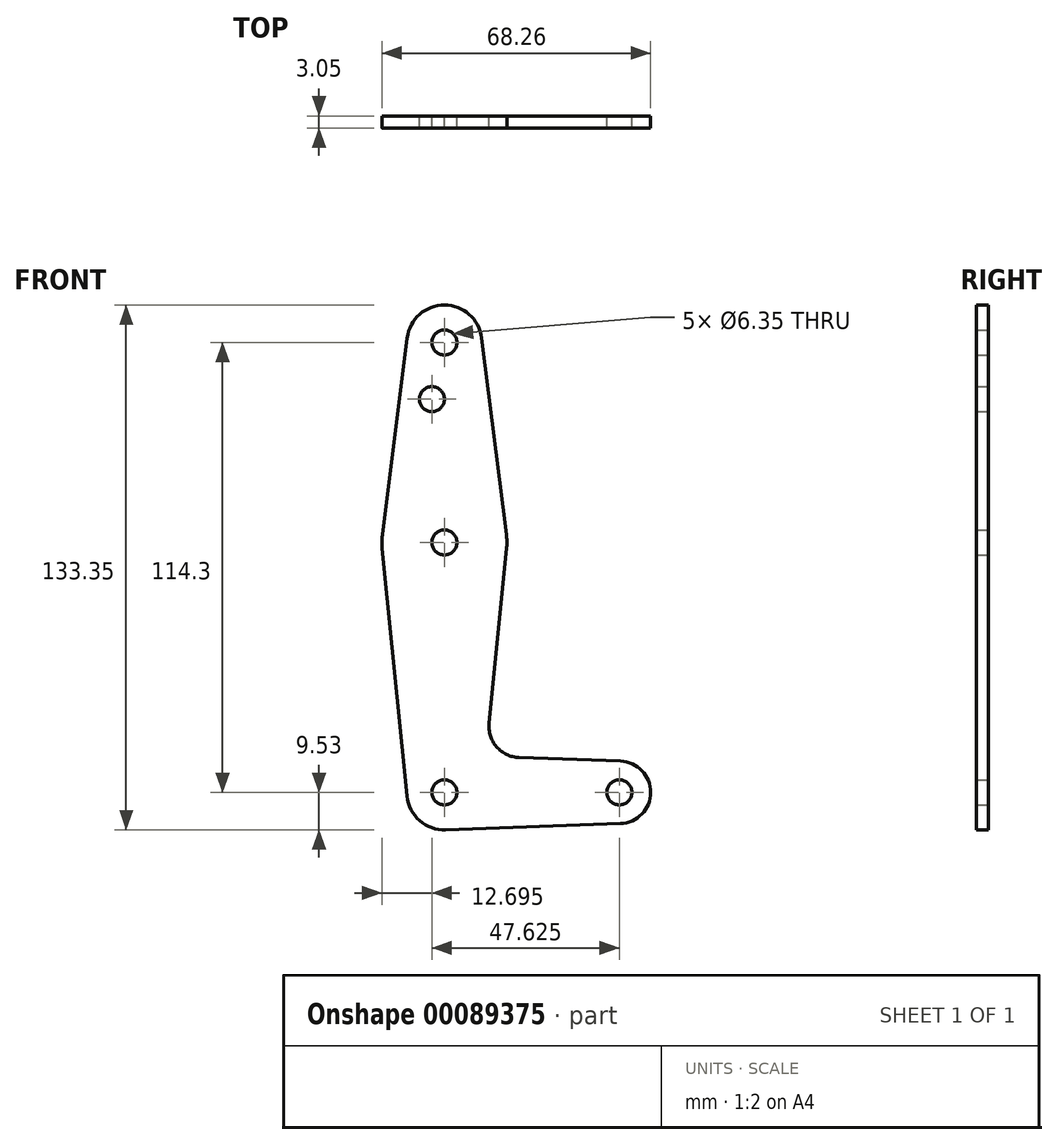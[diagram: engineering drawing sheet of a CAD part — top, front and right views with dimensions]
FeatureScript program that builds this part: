
annotation { "Feature Type Name" : "Feature", "Feature Type Description" : "" }
export const myFeature = defineFeature(function(context is Context, id is Id, definition is map)
    precondition{}
    {
        {
            var Q0;
            Q0=qCreatedBy(makeId("Front.planeOp"),FACE);
            var sketch = newSketch(context, id + "F0", { "sketchPlane" : qUnion([Q0])});
            skCircle(sketch, "E0", {"center": v(0, 0) * mm, "radius": 3.18 * mm});
            skCircle(sketch, "E1", {"center": v(0, 0) * mm, "radius": 15.88 * mm});
            skCircle(sketch, "E2", {"center": v(0, 50.8) * mm, "radius": 9.53 * mm});
            skCircle(sketch, "E3", {"center": v(0, 50.8) * mm, "radius": 3.18 * mm});
            skCircle(sketch, "E4", {"center": v(0, -63.5) * mm, "radius": 3.18 * mm});
            skCircle(sketch, "E5", {"center": v(0, -63.5) * mm, "radius": 9.53 * mm});
            skCircle(sketch, "E6", {"center": v(44.45, -63.5) * mm, "radius": 3.18 * mm});
            skCircle(sketch, "E7", {"center": v(44.45, -63.5) * mm, "radius": 7.94 * mm});
            skLineSegment(sketch, "E8", {"start": v(-9.45, 52) * mm, "end": v(-15.75, 1.98) * mm});
            skLineSegment(sketch, "E9", {"start": v(-15.8, -1.59) * mm, "end": v(-9.48, -64.45) * mm});
            skLineSegment(sketch, "E10", {"start": v(0.34, -73.02) * mm, "end": v(44.73, -71.43) * mm});
            skLineSegment(sketch, "E11", {"start": v(9.45, 52) * mm, "end": v(15.75, 1.98) * mm});
            skLineSegment(sketch, "E12", {"start": v(0, 0) * mm, "end": v(-15.88, 0) * mm, "construction": true});
            skCircle(sketch, "E13", {"center": v(-3.17, 36.4) * mm, "radius": 3.18 * mm});
            skLineSegment(sketch, "E14", {"start": v(0, 50.8) * mm, "end": v(0, 0) * mm, "construction": true});
            skLineSegment(sketch, "E15", {"start": v(18.97, -54.65) * mm, "end": v(44.73, -55.57) * mm});
            skLineSegment(sketch, "E16", {"start": v(15.8, -1.59) * mm, "end": v(11.34, -45.9) * mm});
            skArc(sketch, "E17.filletArc", {"start": v(11.34, -45.9) * mm, "mid": v(13.26, -51.93) * mm, "end": v(18.97, -54.65) * mm});
            skSolve(sketch);
        }
        {
            var Q0;
            Q0 = qSketchRegion(id + "F0", true);
            extrude(context, id + "F1", {"entities" : qUnion([Q0]), "depth" : 3.05 * mm});
        }
    });
